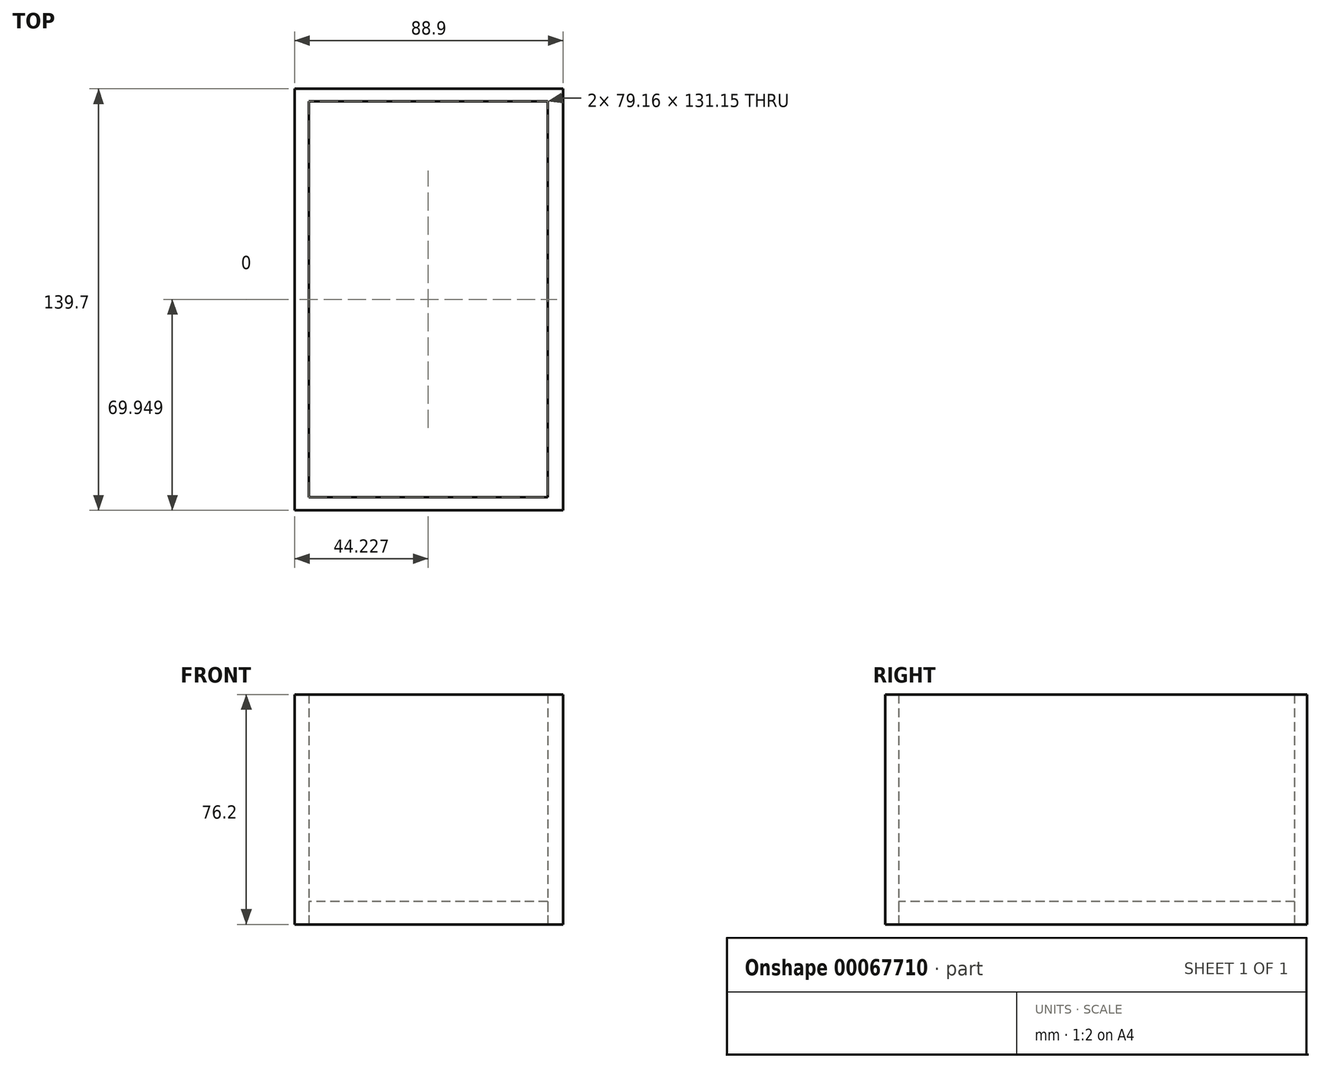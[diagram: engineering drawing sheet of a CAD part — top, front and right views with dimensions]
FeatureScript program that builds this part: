
annotation { "Feature Type Name" : "Feature", "Feature Type Description" : "" }
export const myFeature = defineFeature(function(context is Context, id is Id, definition is map)
    precondition{}
    {
        {
            var Q0;
            Q0=qCreatedBy(makeId("Top.planeOp"),FACE);
            var sketch = newSketch(context, id + "F0", { "sketchPlane" : qUnion([Q0])});
            skLineSegment(sketch, "E0", {"start": v(0, 70.5) * mm, "end": v(-44.03, 70.5) * mm});
            skLineSegment(sketch, "E1", {"start": v(-44.03, 70.5) * mm, "end": v(-44.03, 0) * mm});
            skLineSegment(sketch, "E2", {"start": v(0, 70.5) * mm, "end": v(44.87, 70.5) * mm});
            skLineSegment(sketch, "E3", {"start": v(44.87, 70.5) * mm, "end": v(44.87, 0) * mm});
            skLineSegment(sketch, "E4", {"start": v(0, -69.2) * mm, "end": v(44.87, -69.2) * mm});
            skLineSegment(sketch, "E5", {"start": v(44.87, -69.2) * mm, "end": v(44.87, 0) * mm});
            skLineSegment(sketch, "E6.bottom", {"start": v(-44.03, 70.5) * mm, "end": v(44.87, 70.5) * mm});
            skLineSegment(sketch, "E6.top", {"start": v(-44.03, -69.2) * mm, "end": v(44.87, -69.2) * mm});
            skLineSegment(sketch, "E6.left", {"start": v(-44.03, 70.5) * mm, "end": v(-44.03, -69.2) * mm});
            skLineSegment(sketch, "E6.right", {"start": v(44.87, 70.5) * mm, "end": v(44.87, -69.2) * mm});
            skLineSegment(sketch, "E7", {"start": v(0, 70.5) * mm, "end": v(0.42, 66.32) * mm});
            skPoint(sketch, "E7.endSnap0", {"position": v(0.42, 70.5) * mm});
            skLineSegment(sketch, "E8", {"start": v(0.42, 66.32) * mm, "end": v(-39.38, 66.32) * mm});
            skLineSegment(sketch, "E9", {"start": v(-39.38, 66.32) * mm, "end": v(-39.38, -64.83) * mm});
            skLineSegment(sketch, "E10", {"start": v(-39.38, -64.83) * mm, "end": v(39.78, -64.83) * mm});
            skLineSegment(sketch, "E11", {"start": v(39.78, -64.83) * mm, "end": v(39.78, 66.32) * mm});
            skLineSegment(sketch, "E12", {"start": v(39.78, 66.32) * mm, "end": v(0.42, 66.32) * mm});
            skSolve(sketch);
        }
        {
            var Q0;
            Q0=makeQuery(id+"F0.imprint","IMPRINT",FACE,{"disambiguationData":[TD([[makeQuery(id+"F0.imprint","IMPRINT",EDGE,{"derivedFrom":sQuery(id+"F0.wireOp",EDGE,"E8")}),1.0]])]});
            extrude(context, id + "F1", {"entities" : qUnion([Q0]), "depth" : 7.62 * mm});
        }
        {
            var Q0;
            Q0 = qSketchRegion(id + "F0", true);
            extrude(context, id + "F2", {"entities" : qUnion([Q0]), "depth" : 76.2 * mm});
        }
    });
